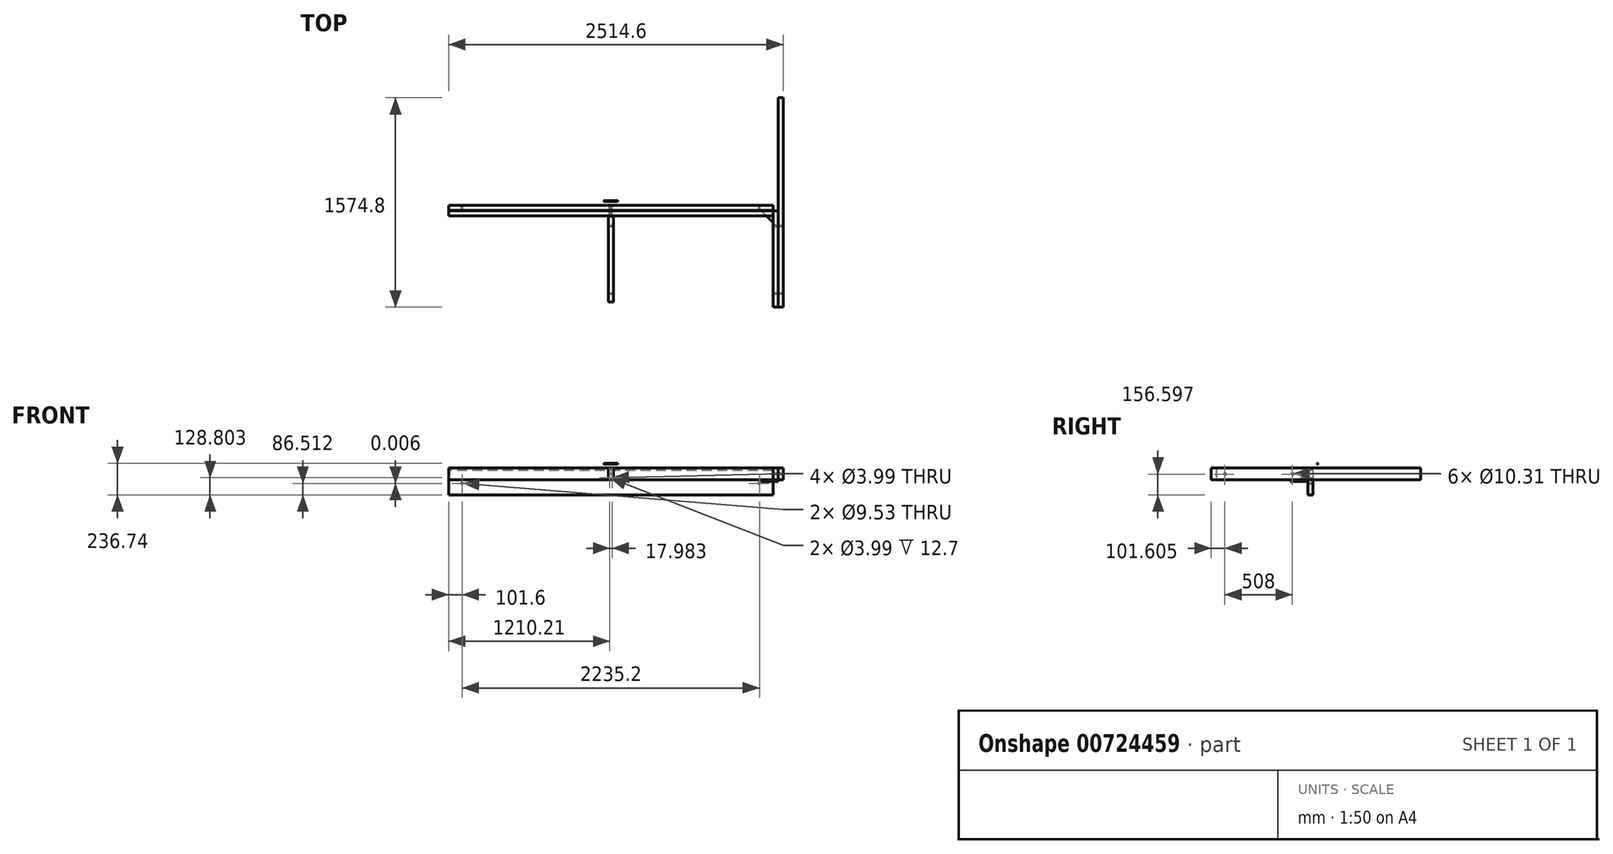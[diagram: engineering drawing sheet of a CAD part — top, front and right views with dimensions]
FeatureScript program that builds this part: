
annotation { "Feature Type Name" : "Feature", "Feature Type Description" : "" }
export const myFeature = defineFeature(function(context is Context, id is Id, definition is map)
    precondition{}
    {
        {
            var Q0;
            Q0=qCreatedBy(makeId("Right.planeOp"),FACE);
            var sketch = newSketch(context, id + "F0", { "sketchPlane" : qUnion([Q0])});
            skLineSegment(sketch, "E0.bottom", {"start": v(0, 0) * mm, "end": v(-38.1, 0) * mm});
            skLineSegment(sketch, "E0.top", {"start": v(0, -184.15) * mm, "end": v(-38.1, -184.15) * mm});
            skLineSegment(sketch, "E0.left", {"start": v(0, 0) * mm, "end": v(0, -184.15) * mm});
            skLineSegment(sketch, "E0.right", {"start": v(-38.1, 0) * mm, "end": v(-38.1, -184.15) * mm});
            skSolve(sketch);
        }
        {
            var Q0;
            Q0 = qSketchRegion(id + "F0", true);
            extrude(context, id + "F1", {"entities" : qUnion([Q0]), "depth" : 2438.4 * mm, "offsetDistance" : 25.4 * mm, "symmetric" : true});
        }
        {
            var Q0;
            Q0=qCreatedBy(makeId("Right.planeOp"),FACE);
            var sketch = newSketch(context, id + "F2", { "sketchPlane" : qUnion([Q0])});
            skLineSegment(sketch, "E1.bottom", {"start": v(-41.27, 19.05) * mm, "end": v(-79.38, 19.05) * mm});
            skLineSegment(sketch, "E1.top", {"start": v(-41.27, -69.85) * mm, "end": v(-79.37, -69.85) * mm});
            skLineSegment(sketch, "E1.left", {"start": v(-41.27, 19.05) * mm, "end": v(-41.27, -69.85) * mm});
            skLineSegment(sketch, "E1.right", {"start": v(-79.38, 19.05) * mm, "end": v(-79.37, -69.85) * mm});
            skSolve(sketch);
        }
        {
            var Q0;
            Q0 = qSketchRegion(id + "F2", true);
            extrude(context, id + "F3", {"entities" : qUnion([Q0]), "depth" : 2438.4 * mm, "offsetDistance" : 25.4 * mm, "symmetric" : true});
        }
        {
            var Q0;
            Q0=makeQuery(id+"F3.opExtrude","CAP_FACE",FACE,{"disambiguationData":[OSD([sQuery(id+"F2.wireOp",EDGE,"E1.bottom"),sQuery(id+"F2.wireOp",EDGE,"E1.top"),sQuery(id+"F2.wireOp",EDGE,"E1.left"),sQuery(id+"F2.wireOp",EDGE,"E1.right")])],"isStart":false});
            var sketch = newSketch(context, id + "F4", { "sketchPlane" : qUnion([Q0])});
            skLineSegment(sketch, "E2.bottom", {"start": v(-41.27, -69.85) * mm, "end": v(-765.18, -69.85) * mm});
            skLineSegment(sketch, "E2.top", {"start": v(-41.27, 19.05) * mm, "end": v(-765.18, 19.05) * mm});
            skLineSegment(sketch, "E2.left", {"start": v(-41.27, -69.85) * mm, "end": v(-41.27, 19.05) * mm});
            skLineSegment(sketch, "E2.right", {"start": v(-765.18, -69.85) * mm, "end": v(-765.18, 19.05) * mm});
            skSolve(sketch);
        }
        {
            var Q0;
            Q0 = qSketchRegion(id + "F4", true);
            extrude(context, id + "F5", {"entities" : qUnion([Q0]), "depth" : 38.1 * mm, "offsetDistance" : 25.4 * mm});
        }
        {
            var Q0;
            Q0=makeQuery(id+"F3.opExtrude","SWEPT_FACE",FACE,{"disambiguationData":[OSD([sQuery(id+"F2.wireOp",EDGE,"E1.right")])]});
            var sketch = newSketch(context, id + "F6", { "sketchPlane" : qUnion([Q0])});
            skLineSegment(sketch, "E3", {"start": v(0, 19.05) * mm, "end": v(0, -69.85) * mm, "construction": true});
            skLineSegment(sketch, "E4.bottom", {"start": v(19.05, 19.05) * mm, "end": v(-19.05, 19.05) * mm});
            skLineSegment(sketch, "E4.top", {"start": v(19.05, -69.85) * mm, "end": v(-19.05, -69.85) * mm});
            skLineSegment(sketch, "E4.left", {"start": v(19.05, 19.05) * mm, "end": v(19.05, -69.85) * mm});
            skLineSegment(sketch, "E4.right", {"start": v(-19.05, 19.05) * mm, "end": v(-19.05, -69.85) * mm});
            skPoint(sketch, "E4.middle", {"position": v(0, -25.4) * mm});
            skSolve(sketch);
        }
        {
            var Q0;
            Q0 = qSketchRegion(id + "F6", true);
            var Q1;
            Q1=makeQuery(id+"F5.opExtrude","SWEPT_FACE",FACE,{"disambiguationData":[OSD([sQuery(id+"F4.wireOp",EDGE,"E2.right")])]});
            extrude(context, id + "F7", {"entities" : qUnion([Q0]), "depth" : 647.7 * mm, "endBoundEntityFace" : qUnion([Q1]), "offsetDistance" : 25.4 * mm});
        }
        {
            var Q0;
            Q0=makeQuery(id+"F1.opExtrude","SWEPT_FACE",FACE,{"disambiguationData":[OSD([sQuery(id+"F0.wireOp",EDGE,"E0.left")])]});
            var sketch = newSketch(context, id + "F8", { "sketchPlane" : qUnion([Q0])});
            skCircle(sketch, "E5", {"center": v(-1117.6, -97.63) * mm, "radius": 4.76 * mm});
            skCircle(sketch, "E6", {"center": v(1117.6, -97.64) * mm, "radius": 4.76 * mm});
            skSolve(sketch);
        }
        {
            var Q0;
            Q0 = qSketchRegion(id + "F8", true);
            extrude(context, id + "F9", {"entities" : qUnion([Q0]), "operationType" : NewBodyOperationType.REMOVE, "endBound" : BoundingType.THROUGH_ALL, "oppositeDirection" : true, "depth" : 25.4 * mm, "offsetDistance" : 25.4 * mm});
        }
        {
            var Q0;
            Q0=makeQuery(id+"F5.opExtrude","SWEPT_FACE",FACE,{"disambiguationData":[OSD([sQuery(id+"F4.wireOp",EDGE,"E2.bottom")])]});
            var sketch = newSketch(context, id + "F10", { "sketchPlane" : qUnion([Q0])});
            skLineSegment(sketch, "E7", {"start": v(1257.3, 41.27) * mm, "end": v(1130.3, 41.27) * mm});
            skLineSegment(sketch, "E8", {"start": v(1257.3, 41.27) * mm, "end": v(1257.3, 168.27) * mm});
            skLineSegment(sketch, "E9", {"start": v(1257.3, 168.28) * mm, "end": v(1130.3, 41.28) * mm});
            skSolve(sketch);
        }
        {
            var Q0;
            {var subQ4=sQuery(id+"F10.wireOp",EDGE,"E8");Q0=makeQuery(id+"F10.imprint","IMPRINT",FACE,{"disambiguationData":[TD([[makeQuery(id+"F10.imprint","IMPRINT",EDGE,{"derivedFrom":subQ4}),1.0]])]});}
            var Q1;
            {var subQ0=sQuery(id+"F10.wireOp",EDGE,"E7");var subQ1=makeQuery(id+"F5.opExtrude","CAP_EDGE",EDGE,{"disambiguationData":[OSD([sQuery(id+"F4.wireOp",EDGE,"E2.bottom")])],"isStart":true});var subQ2=makeQuery(id+"F10.imprint","INTERSECT",VERTEX,{"derivedFrom":[subQ1,subQ0]});Q1=makeQuery(id+"F10.imprint","IMPRINT",FACE,{"disambiguationData":[TD([[makeQuery(id+"F10.imprint","IMPRINT",EDGE,{"disambiguationData":[TD([[subQ2,-1.0]])],"derivedFrom":subQ0}),-1.0]])]});}
            extrude(context, id + "F11", {"entities" : qUnion([Q0, Q1]), "depth" : 13.5 * mm, "offsetDistance" : 25.4 * mm});
        }
        {
            var Q0;
            Q0=makeQuery(id+"F5.opExtrude","SWEPT_FACE",FACE,{"disambiguationData":[OSD([sQuery(id+"F4.wireOp",EDGE,"E2.right")])]});
            var sketch = newSketch(context, id + "F12", { "sketchPlane" : qUnion([Q0])});
            skLineSegment(sketch, "E10.bottom", {"start": v(1257.3, -69.85) * mm, "end": v(1295.4, -69.85) * mm});
            skLineSegment(sketch, "E10.top", {"start": v(1257.3, 19.05) * mm, "end": v(1295.4, 19.05) * mm});
            skLineSegment(sketch, "E10.left", {"start": v(1257.3, -69.85) * mm, "end": v(1257.3, 19.05) * mm});
            skLineSegment(sketch, "E10.right", {"start": v(1295.4, -69.85) * mm, "end": v(1295.4, 19.05) * mm});
            skSolve(sketch);
        }
        {
            var Q0;
            Q0=makeQuery(id+"F12.imprint","IMPRINT",FACE,{"disambiguationData":[TD([[makeQuery(id+"F12.imprint","IMPRINT",EDGE,{"derivedFrom":sQuery(id+"F12.wireOp",EDGE,"E10.bottom")}),1.0]])]});
            extrude(context, id + "F13", {"entities" : qUnion([Q0]), "oppositeDirection" : true, "depth" : 1574.8 * mm, "offsetDistance" : 25.4 * mm});
        }
        {
            var Q0;
            Q0=makeQuery(id+"F13.opExtrude","SWEPT_FACE",FACE,{"disambiguationData":[OSD([sQuery(id+"F12.wireOp",EDGE,"E10.right")])]});
            var sketch = newSketch(context, id + "F14", { "sketchPlane" : qUnion([Q0])});
            skPoint(sketch, "E11", {"position": v(-663.58, -27.55) * mm});
            skPoint(sketch, "E12", {"position": v(-155.58, -27.55) * mm});
            skSolve(sketch);
        }
        {
            var Q0;
            Q0=sQuery(id+"F14.wireOp",VERTEX,"E11");
            var Q1;
            Q1=sQuery(id+"F14.wireOp",VERTEX,"E12");
            var Q2;
            Q2=makeQuery(id+"F5.opExtrude","SWEPT_BODY",BODY,{"disambiguationData":[OSD([sQuery(id+"F4.wireOp",EDGE,"E2.bottom"),sQuery(id+"F4.wireOp",EDGE,"E2.top"),sQuery(id+"F4.wireOp",EDGE,"E2.left"),sQuery(id+"F4.wireOp",EDGE,"E2.right")])]});
            var Q3;
            Q3=makeQuery(id+"F7.opExtrude","SWEPT_BODY",BODY,{"disambiguationData":[OSD([sQuery(id+"F6.wireOp",EDGE,"E4.bottom"),sQuery(id+"F6.wireOp",EDGE,"E4.top"),sQuery(id+"F6.wireOp",EDGE,"E4.left"),sQuery(id+"F6.wireOp",EDGE,"E4.right")])]});
            var Q4;
            Q4=makeQuery(id+"F13.opExtrude","SWEPT_BODY",BODY,{"disambiguationData":[OSD([sQuery(id+"F12.wireOp",EDGE,"E10.bottom"),sQuery(id+"F12.wireOp",EDGE,"E10.top"),sQuery(id+"F12.wireOp",EDGE,"E10.left"),sQuery(id+"F12.wireOp",EDGE,"E10.right")])]});
            hole(context, id + "F15", {"style" : HoleStyle.SIMPLE, "endStyle" : HoleEndStyle.THROUGH, "standardTappedOrClearance" : lookupTablePath({ "fit" : "Normal (ASME)", "standard" : "ANSI", "size" : "3/8", "type" : "Clearance" }), "standardBlindInLast" : lookupTablePath({ "fit" : "Normal", "standard" : "ANSI", "engagement" : "75%", "pitch" : "16 tpi", "size" : "3/8", "type" : "Clearance & tapped" }), "holeDiameter" : 10.3 * mm, "majorDiameter" : 6.35 * mm, "isTappedThrough" : true, "tappedDepth" : 12.7 * mm, "tapClearance" : 3, "locations" : qUnion([Q0, Q1]), "scope" : qUnion([Q2, Q3, Q4]), "startStyle" : HoleStartStyle.PART});
        }
        {
            var Q0;
            Q0=qCreatedBy(makeId("Right.planeOp"),FACE);
            var sketch = newSketch(context, id + "F16", { "sketchPlane" : qUnion([Q0])});
            skCircle(sketch, "E13", {"center": v(33.38, 49.42) * mm, "radius": 3.18 * mm});
            skSolve(sketch);
        }
        {
            var Q0;
            Q0 = qSketchRegion(id + "F16", true);
            extrude(context, id + "F17", {"entities" : qUnion([Q0]), "depth" : 101.6 * mm, "offsetDistance" : 25.4 * mm, "symmetric" : true});
        }
        {
            var Q0;
            Q0=makeQuery(id+"F3.opExtrude","SWEPT_FACE",FACE,{"disambiguationData":[OSD([sQuery(id+"F2.wireOp",EDGE,"E1.left")])]});
            var sketch = newSketch(context, id + "F18", { "sketchPlane" : qUnion([Q0])});
            skLineSegment(sketch, "E14", {"start": v(0, 19.05) * mm, "end": v(0, -69.85) * mm, "construction": true});
            skCircle(sketch, "E15", {"center": v(9, -55.35) * mm, "radius": 2 * mm});
            skCircle(sketch, "E16.MirrorC", {"center": v(-9, -55.35) * mm, "radius": 2 * mm});
            skSolve(sketch);
        }
        {
            var Q0;
            Q0 = qSketchRegion(id + "F18", true);
            extrude(context, id + "F19", {"entities" : qUnion([Q0]), "operationType" : NewBodyOperationType.REMOVE, "oppositeDirection" : true, "depth" : 101.6 * mm, "offsetDistance" : 25.4 * mm, "symmetric" : true});
        }
    });
